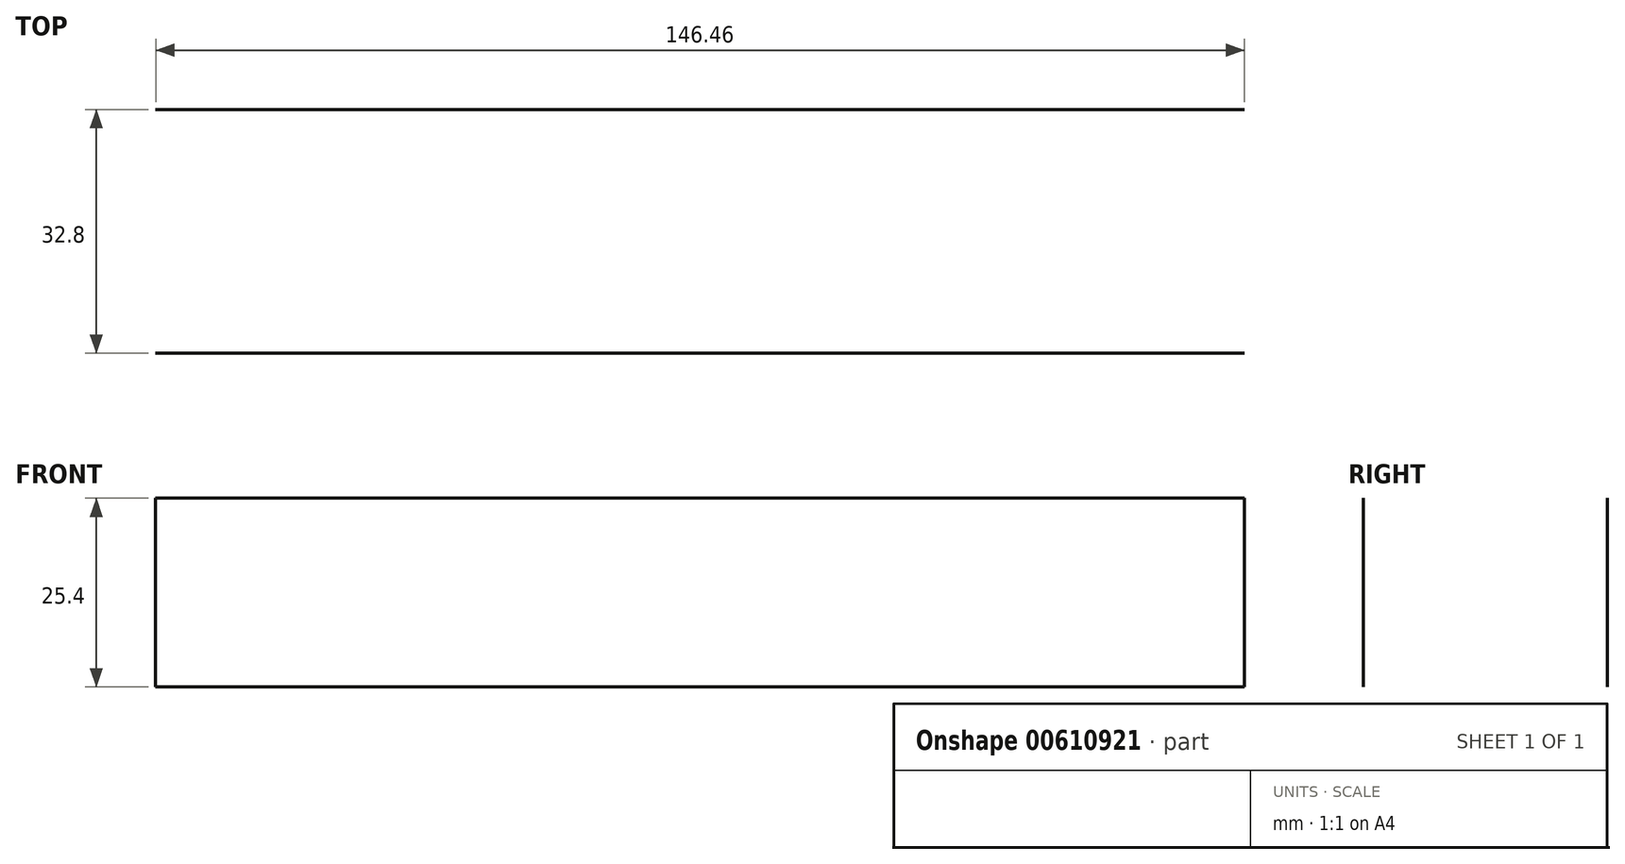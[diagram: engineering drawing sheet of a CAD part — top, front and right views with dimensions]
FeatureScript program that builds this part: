
annotation { "Feature Type Name" : "Feature", "Feature Type Description" : "" }
export const myFeature = defineFeature(function(context is Context, id is Id, definition is map)
    precondition{}
    {
        {
            var Q0;
            Q0=qCreatedBy(makeId("Top.planeOp"),FACE);
            var sketch = newSketch(context, id + "F0", { "sketchPlane" : qUnion([Q0])});
            skLineSegment(sketch, "E0.bottom", {"start": v(73.23, 16.4) * mm, "end": v(-73.23, 16.4) * mm});
            skLineSegment(sketch, "E0.top", {"start": v(73.23, -16.4) * mm, "end": v(-73.23, -16.4) * mm});
            skLineSegment(sketch, "E0.left", {"start": v(73.23, -16.4) * mm, "end": v(73.23, 16.4) * mm});
            skLineSegment(sketch, "E0.right", {"start": v(46.24, 46.6) * mm, "end": v(70.9, 78.06) * mm});
            skPoint(sketch, "E0.middle", {"position": v(0, 0) * mm});
            skSolve(sketch);
        }
        {
            var Q0;
            Q0=sQuery(id+"F0.wireOp",EDGE,"E0.top");
            var Q1;
            Q1=sQuery(id+"F0.wireOp",EDGE,"E0.bottom");
            extrude(context, id + "F1", {"bodyType" : ToolBodyType.SURFACE, "surfaceEntities" : qUnion([Q0, Q1]), "depth" : 25.4 * mm, "offsetDistance" : 25.4 * mm});
        }
    });
